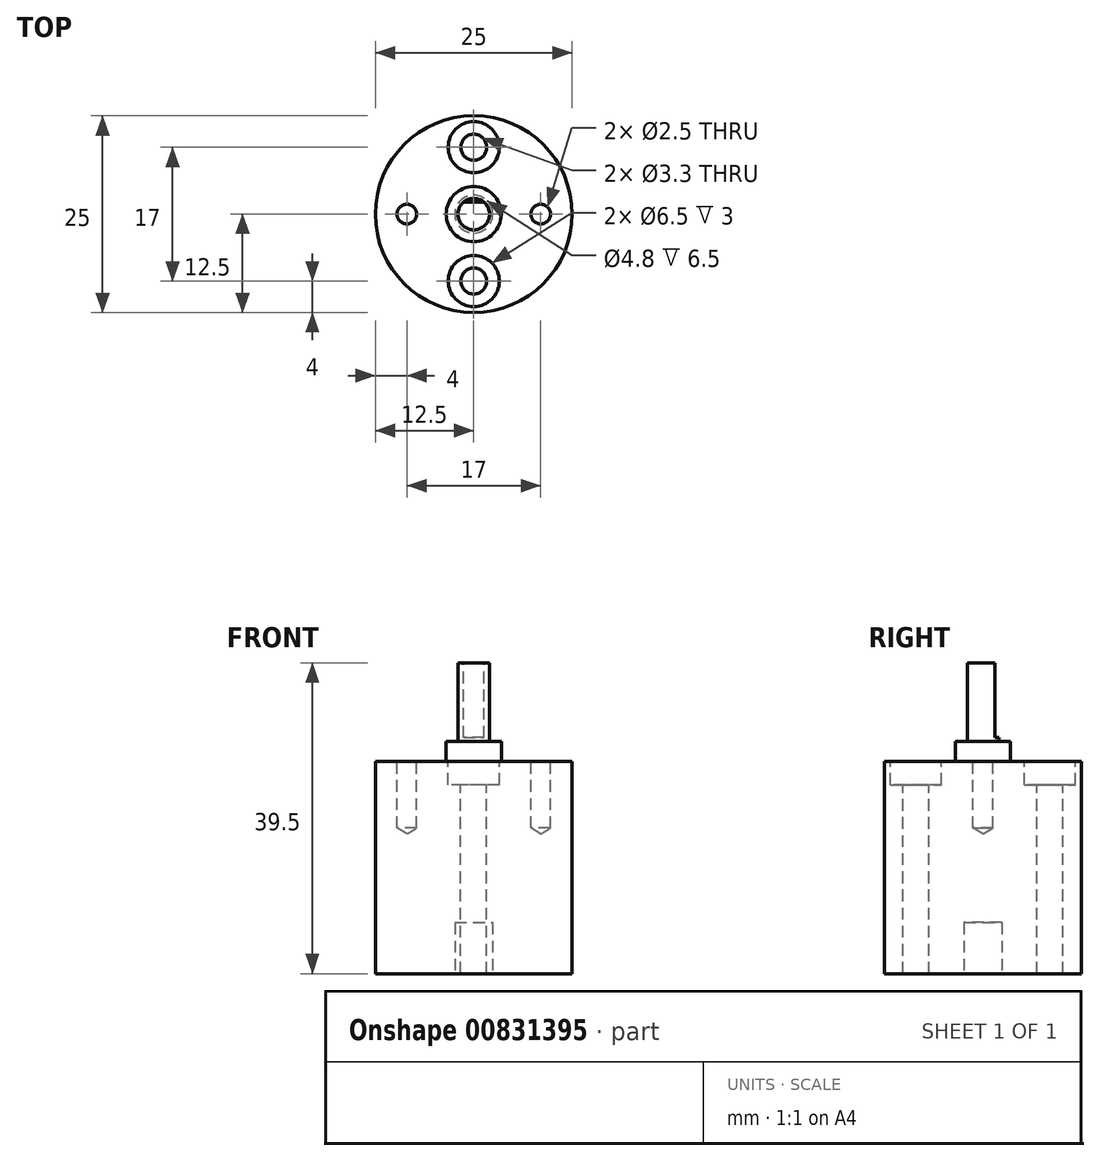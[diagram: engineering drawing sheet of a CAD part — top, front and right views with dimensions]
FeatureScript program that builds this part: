
annotation { "Feature Type Name" : "Feature", "Feature Type Description" : "" }
export const myFeature = defineFeature(function(context is Context, id is Id, definition is map)
    precondition{}
    {
        {
            var Q0;
            Q0=qCreatedBy(makeId("Top.planeOp"),FACE);
            var sketch = newSketch(context, id + "F0", { "sketchPlane" : qUnion([Q0])});
            skCircle(sketch, "E0", {"center": v(0, 0) * mm, "radius": 12.5 * mm});
            skSolve(sketch);
        }
        {
            var Q0;
            Q0 = qSketchRegion(id + "F0", true);
            extrude(context, id + "F1", {"entities" : qUnion([Q0]), "depth" : 27 * mm, "offsetDistance" : 25 * mm});
        }
        {
            var Q0;
            Q0=makeQuery(id+"F1.opExtrude","CAP_FACE",FACE,{"disambiguationData":[OSD([sQuery(id+"F0.wireOp",EDGE,"E0")])],"isStart":false});
            var sketch = newSketch(context, id + "F2", { "sketchPlane" : qUnion([Q0])});
            skCircle(sketch, "E1", {"center": v(0, 0) * mm, "radius": 3.5 * mm});
            skSolve(sketch);
        }
        {
            var Q0;
            Q0 = qSketchRegion(id + "F2", true);
            extrude(context, id + "F3", {"entities" : qUnion([Q0]), "operationType" : NewBodyOperationType.ADD, "depth" : 2.5 * mm, "offsetDistance" : 25 * mm});
        }
        {
            var Q0;
            Q0=makeQuery(id+"F3.opExtrude","CAP_FACE",FACE,{"disambiguationData":[OSD([sQuery(id+"F2.wireOp",EDGE,"E1")])],"isStart":false});
            var sketch = newSketch(context, id + "F4", { "sketchPlane" : qUnion([Q0])});
            skCircle(sketch, "E2", {"center": v(0, 0) * mm, "radius": 2 * mm});
            skSolve(sketch);
        }
        {
            var Q0;
            Q0 = qSketchRegion(id + "F4", true);
            extrude(context, id + "F5", {"entities" : qUnion([Q0]), "operationType" : NewBodyOperationType.ADD, "depth" : 10 * mm, "offsetDistance" : 25 * mm});
        }
        {
            var Q0;
            Q0=makeQuery(id+"F1.opExtrude","CAP_FACE",FACE,{"disambiguationData":[OSD([sQuery(id+"F0.wireOp",EDGE,"E0")])],"isStart":false});
            var sketch = newSketch(context, id + "F6", { "sketchPlane" : qUnion([Q0])});
            skLineSegment(sketch, "E3", {"start": v(-8.5, 0) * mm, "end": v(8.5, 0) * mm, "construction": true});
            skLineSegment(sketch, "E4", {"start": v(0, -8.5) * mm, "end": v(0, 8.5) * mm, "construction": true});
            skSolve(sketch);
        }
        {
            var Q0;
            Q0=sQuery(id+"F6.wireOp",VERTEX,"E3.start");
            var Q1;
            Q1=sQuery(id+"F6.wireOp",VERTEX,"E3.end");
            var Q2;
            Q2=makeQuery(id+"F1.opExtrude","SWEPT_BODY",BODY,{"disambiguationData":[OSD([sQuery(id+"F0.wireOp",EDGE,"E0")])]});
            hole(context, id + "F7", {"style" : HoleStyle.SIMPLE, "endStyle" : HoleEndStyle.BLIND, "standardTappedOrClearance" : lookupTablePath({ "standard" : "ISO", "engagement" : "75%", "pitch" : "0.5 mm", "size" : "M3", "type" : "Tapped" }), "standardBlindInLast" : lookupTablePath({ "standard" : "ISO", "engagement" : "75%", "pitch" : "0.5 mm", "size" : "M3", "type" : "Tapped" }), "holeDiameter" : 2.5 * mm, "majorDiameter" : 3 * mm, "showTappedDepth" : true, "holeDepth" : 8.5 * mm, "isTappedThrough" : true, "tappedDepth" : 7 * mm, "tapClearance" : 3, "startFromSketch" : true, "locations" : qUnion([Q0, Q1]), "scope" : qUnion([Q2])});
        }
        {
            var Q0;
            Q0=sQuery(id+"F6.wireOp",VERTEX,"E4.end");
            var Q1;
            Q1=sQuery(id+"F6.wireOp",VERTEX,"E4.start");
            var Q2;
            Q2=makeQuery(id+"F1.opExtrude","SWEPT_BODY",BODY,{"disambiguationData":[OSD([sQuery(id+"F0.wireOp",EDGE,"E0")])]});
            hole(context, id + "F8", {"style" : HoleStyle.C_BORE, "endStyle" : HoleEndStyle.THROUGH, "standardTappedOrClearance" : lookupTablePath({ "fit" : "Normal", "standard" : "ISO", "size" : "M3", "type" : "Clearance" }), "standardBlindInLast" : lookupTablePath({ "fit" : "Standard", "standard" : "ISO", "size" : "M3", "type" : "Clearance" }), "holeDiameter" : 3.3 * mm, "cBoreDiameter" : 6.5 * mm, "cBoreDepth" : 3 * mm, "majorDiameter" : 3 * mm, "isTappedThrough" : true, "tappedDepth" : 7 * mm, "tapClearance" : 3, "startFromSketch" : true, "locations" : qUnion([Q0, Q1]), "scope" : qUnion([Q2])});
        }
        {
            var Q0;
            Q0=makeQuery(id+"F1.opExtrude","CAP_FACE",FACE,{"disambiguationData":[OSD([sQuery(id+"F0.wireOp",EDGE,"E0")])],"isStart":true});
            var sketch = newSketch(context, id + "F9", { "sketchPlane" : qUnion([Q0])});
            skCircle(sketch, "E5", {"center": v(0, 0) * mm, "radius": 2.4 * mm});
            skSolve(sketch);
        }
        {
            var Q0;
            Q0 = qSketchRegion(id + "F9", true);
            extrude(context, id + "F10", {"entities" : qUnion([Q0]), "operationType" : NewBodyOperationType.REMOVE, "oppositeDirection" : true, "depth" : 6.5 * mm, "offsetDistance" : 25 * mm});
        }
        {
            var Q0;
            Q0=makeQuery(id+"F5.opExtrude","CAP_FACE",FACE,{"disambiguationData":[OSD([sQuery(id+"F4.wireOp",EDGE,"E2")])],"isStart":false});
            var sketch = newSketch(context, id + "F11", { "sketchPlane" : qUnion([Q0])});
            skLineSegment(sketch, "E6.bottom", {"start": v(-1.32, 1.5) * mm, "end": v(1.32, 1.5) * mm});
            skLineSegment(sketch, "E6.top", {"start": v(-1.32, 2) * mm, "end": v(1.32, 2) * mm});
            skLineSegment(sketch, "E6.left", {"start": v(-1.32, 1.5) * mm, "end": v(-1.32, 2) * mm});
            skLineSegment(sketch, "E6.right", {"start": v(1.32, 1.5) * mm, "end": v(1.32, 2) * mm});
            skSolve(sketch);
        }
        {
            var Q0;
            Q0 = qSketchRegion(id + "F11", true);
            extrude(context, id + "F12", {"entities" : qUnion([Q0]), "operationType" : NewBodyOperationType.REMOVE, "oppositeDirection" : true, "depth" : 9.5 * mm, "offsetDistance" : 25 * mm});
        }
    });
